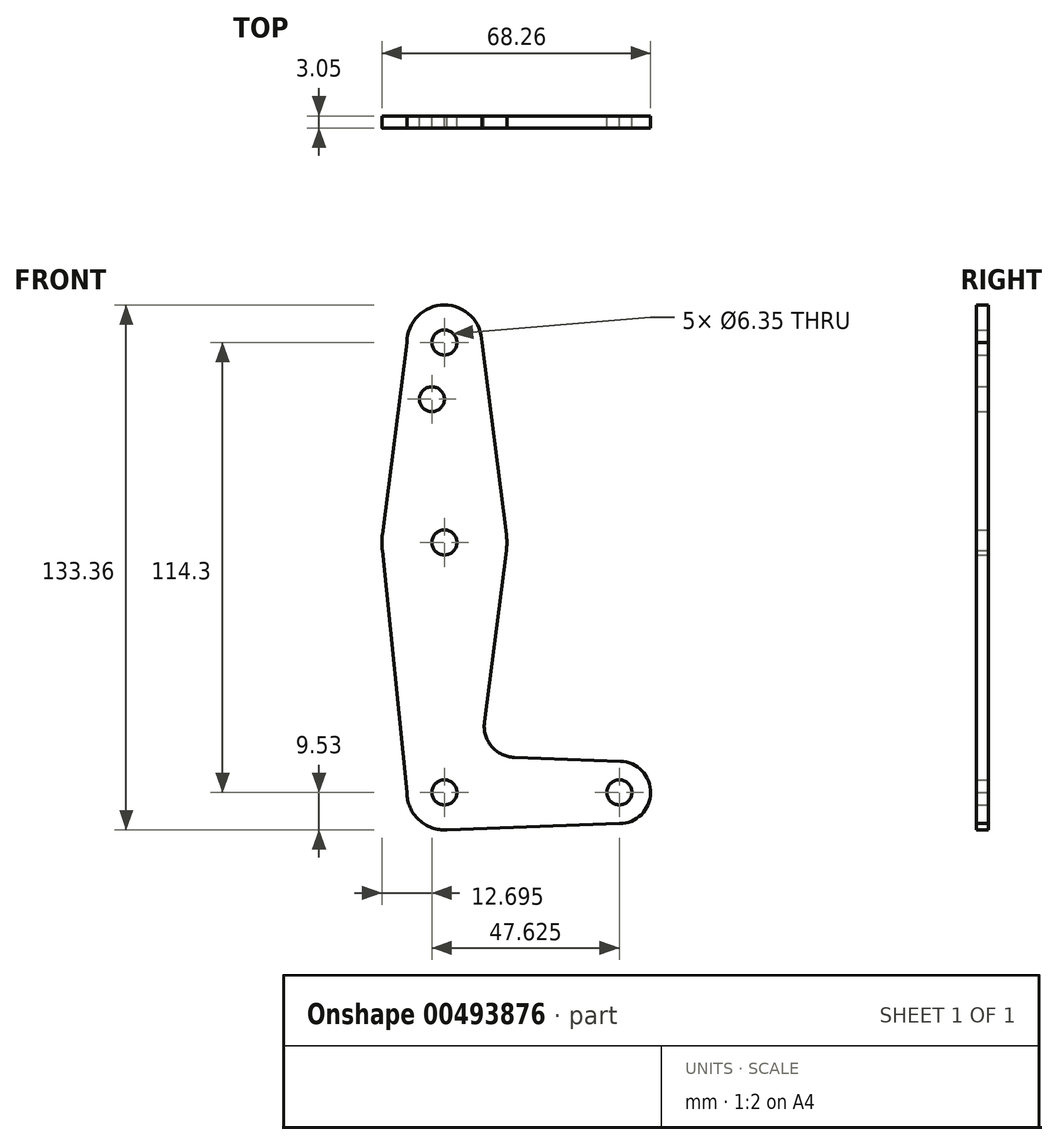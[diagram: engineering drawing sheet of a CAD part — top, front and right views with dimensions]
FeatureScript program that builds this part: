
annotation { "Feature Type Name" : "Feature", "Feature Type Description" : "" }
export const myFeature = defineFeature(function(context is Context, id is Id, definition is map)
    precondition{}
    {
        {
            var Q0;
            Q0=qCreatedBy(makeId("Front.planeOp"),FACE);
            var sketch = newSketch(context, id + "F0", { "sketchPlane" : qUnion([Q0])});
            skLineSegment(sketch, "E0", {"start": v(0, 0) * mm, "end": v(0, 114.3) * mm, "construction": true});
            skLineSegment(sketch, "E1", {"start": v(0, 0) * mm, "end": v(44.45, 0) * mm, "construction": true});
            skCircle(sketch, "E2", {"center": v(0, 114.3) * mm, "radius": 9.53 * mm});
            skCircle(sketch, "E3", {"center": v(0, 63.5) * mm, "radius": 15.88 * mm});
            skCircle(sketch, "E4", {"center": v(0, 0) * mm, "radius": 9.53 * mm});
            skCircle(sketch, "E5", {"center": v(44.45, 0) * mm, "radius": 7.94 * mm});
            skLineSegment(sketch, "E6", {"start": v(-9.53, 114.3) * mm, "end": v(-15.75, 65.5) * mm});
            skLineSegment(sketch, "E7", {"start": v(9.52, 114.3) * mm, "end": v(15.75, 65.5) * mm});
            skLineSegment(sketch, "E8", {"start": v(-15.75, 61.5) * mm, "end": v(-9.53, 0) * mm});
            skLineSegment(sketch, "E9", {"start": v(15.75, 61.5) * mm, "end": v(10.18, 17.84) * mm});
            skLineSegment(sketch, "E10", {"start": v(17.78, 8.9) * mm, "end": v(44.73, 7.93) * mm});
            skCircle(sketch, "E11", {"center": v(0, 114.3) * mm, "radius": 3.18 * mm});
            skCircle(sketch, "E12", {"center": v(-3.18, 99.89) * mm, "radius": 3.18 * mm});
            skCircle(sketch, "E13", {"center": v(0, 63.5) * mm, "radius": 3.18 * mm});
            skCircle(sketch, "E14", {"center": v(0, 0) * mm, "radius": 3.18 * mm});
            skCircle(sketch, "E15", {"center": v(44.45, 0) * mm, "radius": 3.18 * mm});
            skLineSegment(sketch, "E16", {"start": v(0, -9.52) * mm, "end": v(44.45, -7.94) * mm});
            skArc(sketch, "E17.filletArc", {"start": v(10.18, 17.84) * mm, "mid": v(12, 11.69) * mm, "end": v(17.78, 8.9) * mm});
            skSolve(sketch);
        }
        {
            var Q0;
            Q0 = qSketchRegion(id + "F0", true);
            extrude(context, id + "F1", {"entities" : qUnion([Q0]), "depth" : 3.05 * mm});
        }
    });
